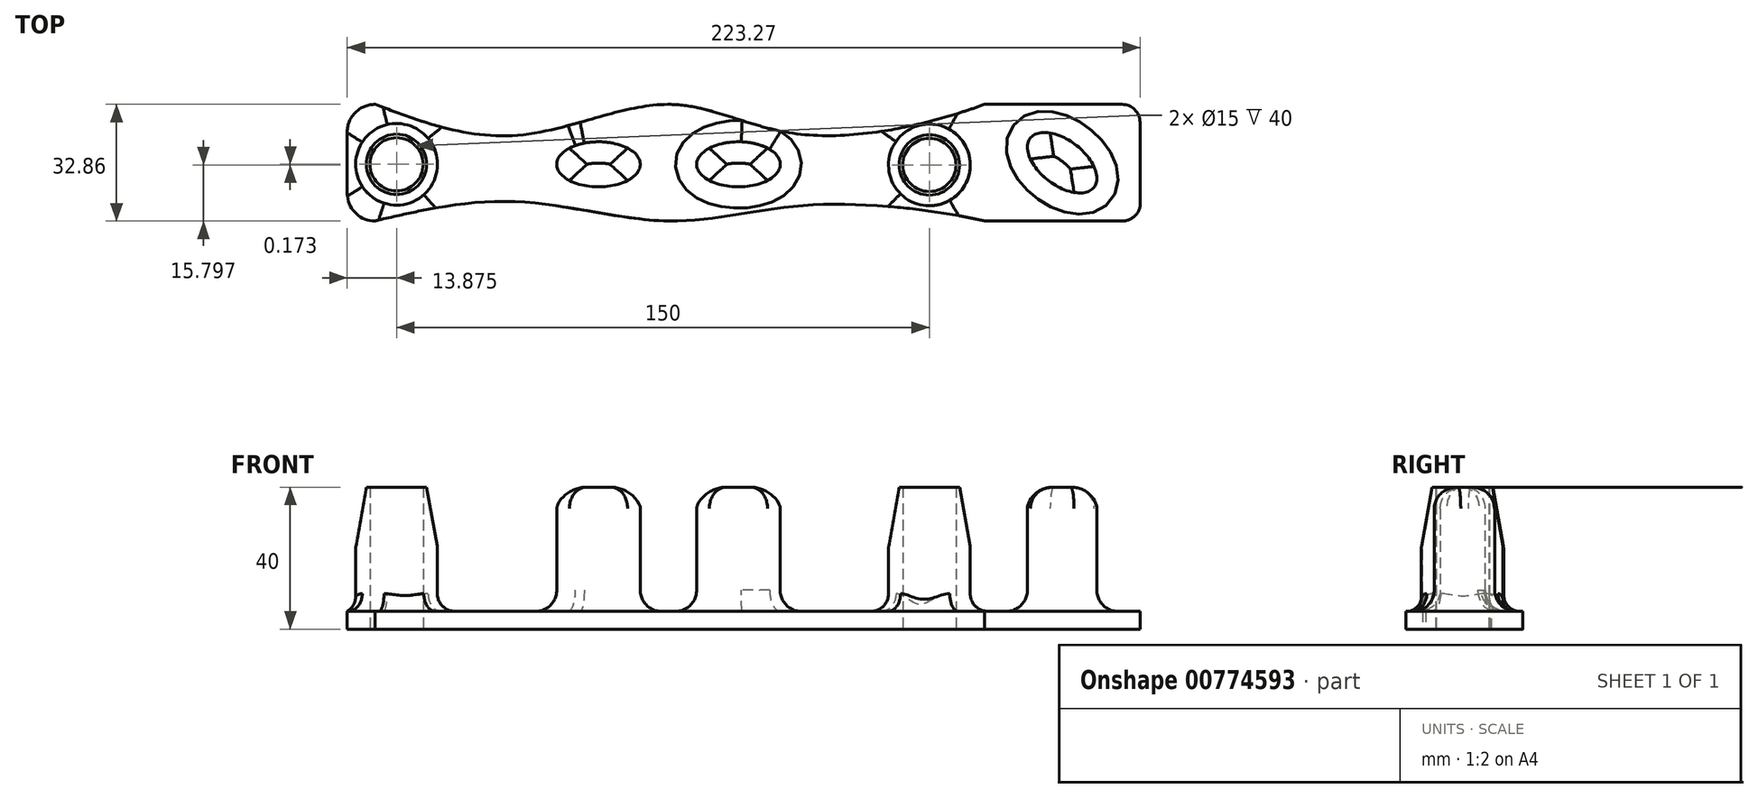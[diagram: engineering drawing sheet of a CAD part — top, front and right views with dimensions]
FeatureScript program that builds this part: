
annotation { "Feature Type Name" : "Feature", "Feature Type Description" : "" }
export const myFeature = defineFeature(function(context is Context, id is Id, definition is map)
    precondition{}
    {
        {
            var Q0;
            Q0=qCreatedBy(makeId("Top.planeOp"),FACE);
            var sketch = newSketch(context, id + "F0", { "sketchPlane" : qUnion([Q0])});
            skLineSegment(sketch, "E0.top", {"start": v(0, -15.96) * mm, "end": v(0.22, -15.96) * mm});
            skLineSegment(sketch, "E0.left", {"start": v(-90.43, 9.12) * mm, "end": v(-90.43, -8.18) * mm});
            skCircle(sketch, "E1", {"center": v(-76.56, 0) * mm, "radius": 7.5 * mm});
            skCircle(sketch, "E2", {"center": v(73.44, -0.17) * mm, "radius": 7.5 * mm});
            skPoint(sketch, "E3.visualSharp", {"position": v(-90.43, 11.72) * mm});
            skArc(sketch, "E3.filletArc", {"start": v(-82.44, 16.89) * mm, "mid": v(-88.07, 14.7) * mm, "end": v(-90.43, 9.12) * mm});
            skPoint(sketch, "E4.visualSharp", {"position": v(-90.43, -15.96) * mm});
            skArc(sketch, "E4.filletArc", {"start": v(-90.43, -8.18) * mm, "mid": v(-88.15, -13.68) * mm, "end": v(-82.66, -15.96) * mm});
            skPoint(sketch, "E5.visualSharp", {"position": v(89.57, -15.96) * mm});
            skLineSegment(sketch, "E6.bottom", {"start": v(-0.22, 16.89) * mm, "end": v(0, 16.89) * mm});
            skLineSegment(sketch, "E6.right", {"start": v(132.7, 16.89) * mm, "end": v(132.86, -15.96) * mm});
            skPoint(sketch, "E7.endDerivative.orphan", {"position": v(91.69, 0) * mm});
            skLineSegment(sketch, "E8", {"start": v(88.91, 16.89) * mm, "end": v(132.86, -15.96) * mm, "construction": true});
            skLineSegment(sketch, "E9", {"start": v(88.91, -15.96) * mm, "end": v(132.7, 16.89) * mm, "construction": true});
            skLineSegment(sketch, "E10", {"start": v(110.81, 16.89) * mm, "end": v(110.81, -15.96) * mm, "construction": true});
            skPoint(sketch, "E10.startSnap0", {"position": v(110.81, 0.47) * mm});
            skFitSpline(sketch, "E11", {"points": [v(-82.44, 16.89) * mm, v(0, 16.89) * mm], "startDerivative": vector(24.64, 38.33) * mm, "endDerivative": vector(86.8, 0.1) * mm});
            skFitSpline(sketch, "E12", {"points": [v(-82.44, 16.89) * mm, v(-41.42, 8.3) * mm, v(0, 16.89) * mm, v(35.15, 8.73) * mm, v(88.91, 16.89) * mm], "startDerivative": vector(175.46, -68.8) * mm, "endDerivative": vector(183.15, 67.32) * mm});
            skPoint(sketch, "E13.2.internal.snap0", {"position": v(0.22, -15.96) * mm});
            skFitSpline(sketch, "E13", {"points": [v(-82.66, -15.96) * mm, v(-42.37, -10.54) * mm, v(0, -15.96) * mm, v(37.13, -11.66) * mm, v(88.91, -15.96) * mm], "startDerivative": vector(173.45, 40.32) * mm, "endDerivative": vector(176.54, -39.95) * mm});
            skLineSegment(sketch, "E14.trimOffspring", {"start": v(88.91, 16.89) * mm, "end": v(132.7, 16.89) * mm});
            skLineSegment(sketch, "E15.trimOffspring", {"start": v(88.91, -15.96) * mm, "end": v(132.86, -15.96) * mm});
            skLineSegment(sketch, "E16.trimOffspring", {"start": v(83.09, -15.96) * mm, "end": v(88.91, -15.96) * mm});
            skCircle(sketch, "E17", {"center": v(-76.56, 0) * mm, "radius": 11.5 * mm});
            skCircle(sketch, "E18", {"center": v(73.44, -0.17) * mm, "radius": 11.5 * mm});
            skEllipse(sketch, "E19", {"center": v(-19.7, 0) * mm, "majorRadius": 11.76 * mm, "minorRadius": 6.35 * mm, "majorAxis": v(1, 0)});
            skEllipse(sketch, "E20.MirrorC", {"center": v(19.7, 0) * mm, "majorRadius": 11.76 * mm, "minorRadius": 6.35 * mm, "majorAxis": v(-1, 0)});
            skEllipse(sketch, "E21", {"center": v(110.81, 0.47) * mm, "majorRadius": 11.33 * mm, "minorRadius": 6.32 * mm, "majorAxis": v(-0.8, 0.6)});
            skSolve(sketch);
        }
        {
            var Q0;
            Q0=makeQuery(id+"F0.imprint","IMPRINT",FACE,{"disambiguationData":[TD([[makeQuery(id+"F0.imprint","IMPRINT",EDGE,{"derivedFrom":sQuery(id+"F0.wireOp",EDGE,"E0.bottom")}),-1.0]])]});
            var Q1;
            Q1=makeQuery(id+"F0.imprint","IMPRINT",FACE,{"disambiguationData":[TD([[makeQuery(id+"F0.imprint","IMPRINT",EDGE,{"derivedFrom":sQuery(id+"F0.wireOp",EDGE,"E0.top")}),1.0]])]});
            var Q2;
            Q2=makeQuery(id+"F0.imprint","IMPRINT",FACE,{"disambiguationData":[TD([[makeQuery(id+"F0.imprint","IMPRINT",EDGE,{"derivedFrom":sQuery(id+"F0.wireOp",EDGE,"E0.left")}),1.0]])]});
            extrude(context, id + "F1", {"entities" : qUnion([Q0, Q1, Q2]), "depth" : 5 * mm, "offsetDistance" : 25 * mm});
        }
        {
            var Q0;
            Q0=makeQuery(id+"F0.imprint","IMPRINT",FACE,{"disambiguationData":[TD([[makeQuery(id+"F0.imprint","IMPRINT",EDGE,{"derivedFrom":sQuery(id+"F0.wireOp",EDGE,"E1")}),-1.0]])]});
            var Q1;
            Q1=makeQuery(id+"F0.imprint","IMPRINT",FACE,{"disambiguationData":[TD([[makeQuery(id+"F0.imprint","IMPRINT",EDGE,{"derivedFrom":sQuery(id+"F0.wireOp",EDGE,"E2")}),-1.0]])]});
            extrude(context, id + "F2", {"entities" : qUnion([Q0, Q1]), "operationType" : NewBodyOperationType.ADD, "depth" : 40 * mm, "offsetDistance" : 25 * mm});
        }
        {
            var Q0;
            Q0=makeQuery(id+"F2.opExtrude","CAP_EDGE",EDGE,{"disambiguationData":[OSD([sQuery(id+"F0.wireOp",EDGE,"E17")])],"isStart":false});
            var Q1;
            Q1=makeQuery(id+"F2.opExtrude","CAP_EDGE",EDGE,{"disambiguationData":[OSD([sQuery(id+"F0.wireOp",EDGE,"E18")])],"isStart":false});
            chamfer(context, id + "F3", {"entities" : qUnion([Q0, Q1]), "chamferType" : ChamferType.OFFSET_ANGLE, "width" : 3 * mm, "oppositeDirection" : false, "angle" : 80 * degree, "tangentPropagation" : true});
        }
        {
            var Q0;
            Q0=makeQuery(id+"F0.imprint","IMPRINT",FACE,{"disambiguationData":[TD([[makeQuery(id+"F0.imprint","IMPRINT",EDGE,{"derivedFrom":sQuery(id+"F0.wireOp",EDGE,"E19")}),1.0]])]});
            var Q1;
            Q1=makeQuery(id+"F0.imprint","IMPRINT",FACE,{"disambiguationData":[TD([[makeQuery(id+"F0.imprint","IMPRINT",EDGE,{"derivedFrom":sQuery(id+"F0.wireOp",EDGE,"E20.MirrorC")}),1.0]])]});
            var Q2;
            Q2=makeQuery(id+"F0.imprint","IMPRINT",FACE,{"disambiguationData":[TD([[makeQuery(id+"F0.imprint","IMPRINT",EDGE,{"derivedFrom":sQuery(id+"F0.wireOp",EDGE,"E21")}),1.0]])]});
            extrude(context, id + "F4", {"entities" : qUnion([Q0, Q1, Q2]), "operationType" : NewBodyOperationType.ADD, "depth" : 40 * mm, "offsetDistance" : 25 * mm});
        }
        {
            var Q0;
            Q0=makeQuery(id+"F4.opExtrude","CAP_FACE",FACE,{"disambiguationData":[OSD([sQuery(id+"F0.wireOp",EDGE,"E19")])],"isStart":false});
            var Q1;
            Q1=makeQuery(id+"F4.opExtrude","CAP_FACE",FACE,{"disambiguationData":[OSD([sQuery(id+"F0.wireOp",EDGE,"E20.MirrorC")])],"isStart":false});
            var Q2;
            Q2=makeQuery(id+"F4.opExtrude","SWEPT_FACE",FACE,{"disambiguationData":[OSD([sQuery(id+"F0.wireOp",EDGE,"E20.MirrorC")])]});
            var Q3;
            Q3=makeQuery(id+"F4.opExtrude","SWEPT_FACE",FACE,{"disambiguationData":[OSD([sQuery(id+"F0.wireOp",EDGE,"E19")])]});
            var Q4;
            Q4=makeQuery(id+"F4.opExtrude","SWEPT_FACE",FACE,{"disambiguationData":[OSD([sQuery(id+"F0.wireOp",EDGE,"E21")])]});
            var Q5;
            Q5=makeQuery(id+"F4.opExtrude","CAP_FACE",FACE,{"disambiguationData":[OSD([sQuery(id+"F0.wireOp",EDGE,"E21")])],"isStart":false});
            fillet(context, id + "F5", {"entities" : qUnion([Q0, Q1, Q2, Q3, Q4, Q5]), "radius" : 6 * mm, "tangentPropagation" : true, "allowEdgeOverflow" : false});
        }
        {
            var Q0;
            Q0=makeQuery(id+"F2.opExtrude","SWEPT_FACE",FACE,{"disambiguationData":[OSD([sQuery(id+"F0.wireOp",EDGE,"E17")])]});
            var Q1;
            Q1=makeQuery(id+"F2.opExtrude","SWEPT_FACE",FACE,{"disambiguationData":[OSD([sQuery(id+"F0.wireOp",EDGE,"E18")])]});
            fillet(context, id + "F6", {"entities" : qUnion([Q0, Q1]), "radius" : 5 * mm, "tangentPropagation" : true, "allowEdgeOverflow" : false});
        }
        {
            var Q0;
            Q0=makeQuery(id+"F1.opExtrude","SWEPT_EDGE",EDGE,{"disambiguationData":[OSD([sQuery(id+"F0.wireOp",EDGE,"E6.right"),sQuery(id+"F0.wireOp",EDGE,"E15.trimOffspring")])]});
            var Q1;
            Q1=makeQuery(id+"F1.opExtrude","SWEPT_EDGE",EDGE,{"disambiguationData":[OSD([sQuery(id+"F0.wireOp",EDGE,"E6.right"),sQuery(id+"F0.wireOp",EDGE,"E14.trimOffspring")])]});
            fillet(context, id + "F7", {"entities" : qUnion([Q0, Q1]), "radius" : 5 * mm, "tangentPropagation" : true, "allowEdgeOverflow" : false});
        }
    });
